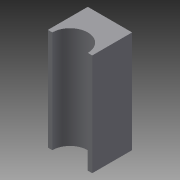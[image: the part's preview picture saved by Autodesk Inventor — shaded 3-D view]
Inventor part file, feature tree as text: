
AUTODESK INVENTOR PART (.ipt)
format: ipt  version: 2015 SP2 (Build 190223200, 223)  size: 77,824 bytes
history: native  units: mm
features: sketch x2, extrude x1, hole x1
ambient origin geometry x8: Origin, YZ Plane, XZ Plane, XY Plane, X Axis, Y Axis, Z Axis, Center Point
bodies: Solid1 (feature_tree)
feature tree (4):
  extrude  "Extrusion1"  Depth=23.0mm
  hole  "Hole1"  [1 undecoded]
  sketch  "Sketch1"  dims[d0=10.0mm d1=23.0mm]
  sketch  "Sketch4"  dims[d2=9.0mm d3=0.0mm d11=8.0mm d12=8.0mm d13=6.0mm d14=4.0mm d15=2.0mm d16=90.0deg d17=8.0mm d18=20.594885mm]
note: 1 required parameter value undecoded (feature->parameter linkage not recoverable at this tier; creation-order binding heuristic only, values carry confidence <= 0.55)
